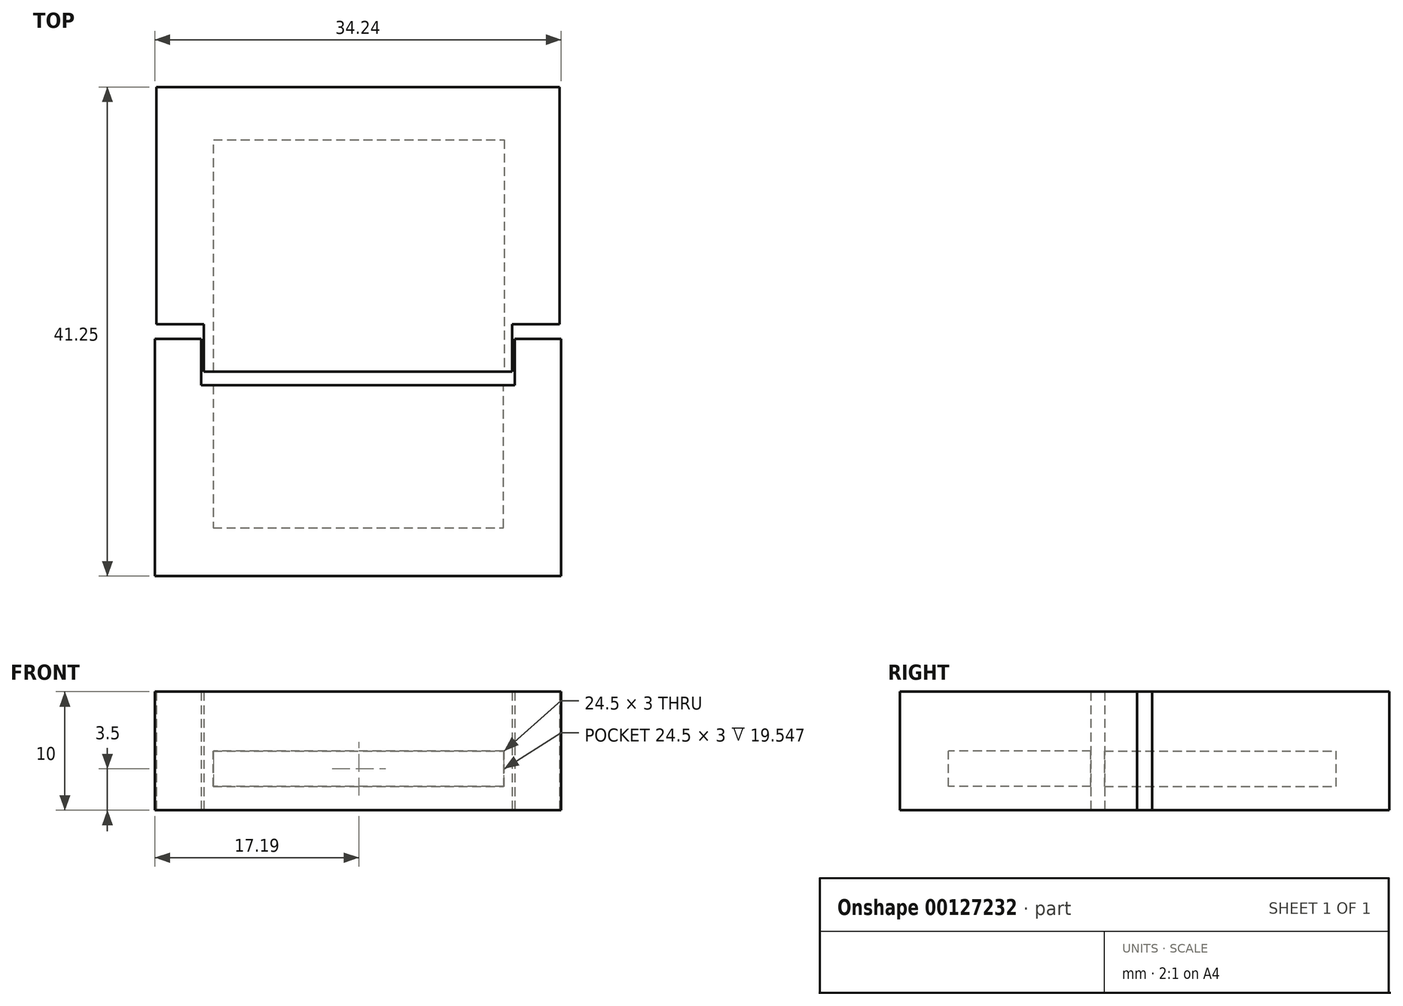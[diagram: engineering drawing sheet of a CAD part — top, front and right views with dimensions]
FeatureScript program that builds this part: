
annotation { "Feature Type Name" : "Feature", "Feature Type Description" : "" }
export const myFeature = defineFeature(function(context is Context, id is Id, definition is map)
    precondition{}
    {
        {
            var Q0;
            Q0=qCreatedBy(makeId("Top.planeOp"),FACE);
            var sketch = newSketch(context, id + "F0", { "sketchPlane" : qUnion([Q0])});
            skLineSegment(sketch, "E0", {"start": v(13, 0) * mm, "end": v(13, 4) * mm});
            skLineSegment(sketch, "E1", {"start": v(13, 4) * mm, "end": v(17, 4) * mm});
            skLineSegment(sketch, "E2", {"start": v(13.22, 2.75) * mm, "end": v(17.12, 2.75) * mm});
            skLineSegment(sketch, "E3", {"start": v(0, -1.15) * mm, "end": v(13.22, -1.15) * mm});
            skLineSegment(sketch, "E4", {"start": v(13.22, -1.15) * mm, "end": v(13.22, 2.75) * mm});
            skLineSegment(sketch, "E5.MirrorCS", {"start": v(-17, 4) * mm, "end": v(-17, 24) * mm});
            skLineSegment(sketch, "E6.MirrorCS", {"start": v(-13, 4) * mm, "end": v(-17, 4) * mm});
            skLineSegment(sketch, "E7.MirrorCS", {"start": v(-13, 0) * mm, "end": v(-13, 4) * mm});
            skLineSegment(sketch, "E8.MirrorCS", {"start": v(0, -1.15) * mm, "end": v(-13.22, -1.15) * mm});
            skLineSegment(sketch, "E9.MirrorCS", {"start": v(-13.22, 2.75) * mm, "end": v(-17.12, 2.75) * mm});
            skLineSegment(sketch, "E10.MirrorCS", {"start": v(-13.22, -1.15) * mm, "end": v(-13.22, 2.75) * mm});
            skLineSegment(sketch, "E11", {"start": v(-13, 0) * mm, "end": v(13, 0) * mm});
            skLineSegment(sketch, "E12", {"start": v(17, 4) * mm, "end": v(17, 24) * mm});
            skLineSegment(sketch, "E13", {"start": v(17, 24) * mm, "end": v(-17, 24) * mm});
            skLineSegment(sketch, "E14", {"start": v(17.12, 2.75) * mm, "end": v(17.12, -17.25) * mm});
            skLineSegment(sketch, "E15", {"start": v(17.12, -17.25) * mm, "end": v(-17.12, -17.25) * mm});
            skLineSegment(sketch, "E16", {"start": v(-17.12, 2.75) * mm, "end": v(-17.12, -17.25) * mm});
            skSolve(sketch);
        }
        {
            var Q0;
            Q0 = qSketchRegion(id + "F0", true);
            extrude(context, id + "F1", {"entities" : qUnion([Q0]), "depth" : 10 * mm});
        }
        {
            var Q0;
            Q0=qCreatedBy(makeId("Top.planeOp"),FACE);
            cPlane(context, id + "F2", {"entities" : qUnion([Q0]), "cplaneType" : CPlaneType.OFFSET, "offset" : 5 * mm, "width" : 150 * mm, "height" : 150 * mm});
        }
        {
            var Q0;
            Q0=qCreatedBy(id+"F2.planeOp",FACE);
            var sketch = newSketch(context, id + "F3", { "sketchPlane" : qUnion([Q0])});
            skLineSegment(sketch, "E17", {"start": v(-12.18, 0) * mm, "end": v(-12.18, 19.55) * mm});
            skLineSegment(sketch, "E18", {"start": v(-12.18, 19.55) * mm, "end": v(12.32, 19.55) * mm});
            skLineSegment(sketch, "E19", {"start": v(12.32, 19.55) * mm, "end": v(12.32, 0) * mm});
            skLineSegment(sketch, "E20", {"start": v(12.32, 0) * mm, "end": v(-12.18, 0) * mm});
            skLineSegment(sketch, "E21", {"start": v(-12.18, 0) * mm, "end": v(12.32, 0) * mm});
            skSolve(sketch);
        }
        {
            var Q0;
            Q0 = qSketchRegion(id + "F3", true);
            extrude(context, id + "F4", {"entities" : qUnion([Q0]), "operationType" : NewBodyOperationType.REMOVE, "oppositeDirection" : true, "depth" : 3 * mm});
        }
        {
            var Q0;
            Q0=qCreatedBy(id+"F2.planeOp",FACE);
            var sketch = newSketch(context, id + "F5", { "sketchPlane" : qUnion([Q0])});
            skLineSegment(sketch, "E22", {"start": v(-12.22, -13.17) * mm, "end": v(12.28, -13.17) * mm});
            skLineSegment(sketch, "E23", {"start": v(12.28, -13.17) * mm, "end": v(12.28, -0.9) * mm});
            skLineSegment(sketch, "E24", {"start": v(12.28, -0.9) * mm, "end": v(-12.22, -0.9) * mm});
            skLineSegment(sketch, "E25", {"start": v(-12.22, -0.9) * mm, "end": v(-12.22, -13.17) * mm});
            skSolve(sketch);
        }
        {
            var Q0;
            Q0 = qSketchRegion(id + "F5", true);
            extrude(context, id + "F6", {"entities" : qUnion([Q0]), "operationType" : NewBodyOperationType.REMOVE, "oppositeDirection" : true, "depth" : 3 * mm});
        }
    });
